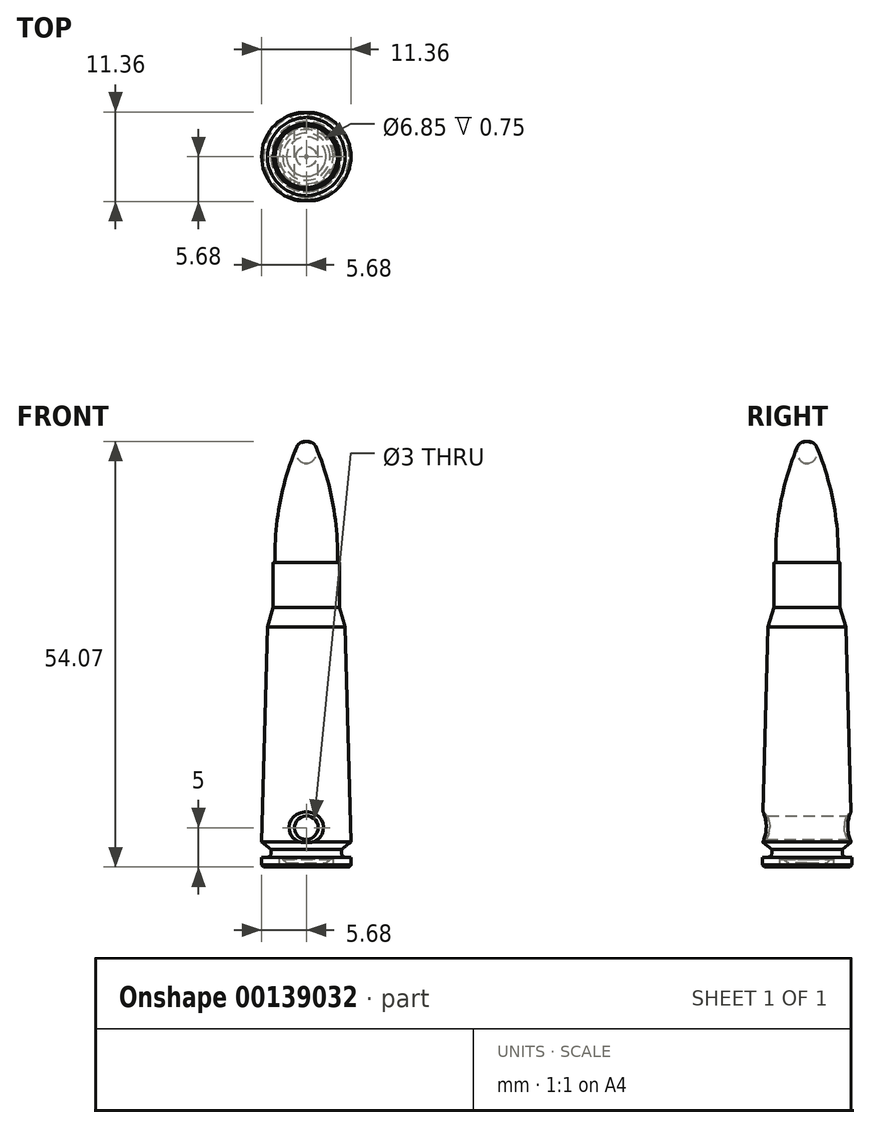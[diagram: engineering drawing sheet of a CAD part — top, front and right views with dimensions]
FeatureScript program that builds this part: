
annotation { "Feature Type Name" : "Feature", "Feature Type Description" : "" }
export const myFeature = defineFeature(function(context is Context, id is Id, definition is map)
    precondition{}
    {
        {
            var Q0;
            Q0=qCreatedBy(makeId("Front.planeOp"),FACE);
            var sketch = newSketch(context, id + "F0", { "sketchPlane" : qUnion([Q0])});
            skLineSegment(sketch, "E0", {"start": v(-11.63, 0) * mm, "end": v(20.36, 0) * mm, "construction": true});
            skLineSegment(sketch, "E1", {"start": v(0, -4.88) * mm, "end": v(0, 19.51) * mm, "construction": true});
            skLineSegment(sketch, "E2", {"start": v(0, 0) * mm, "end": v(-5.42, 0) * mm});
            skLineSegment(sketch, "E3", {"start": v(-5.42, 0) * mm, "end": v(-5.68, 0.25) * mm});
            skLineSegment(sketch, "E4", {"start": v(-5.68, 0.25) * mm, "end": v(-5.68, 1.25) * mm});
            skLineSegment(sketch, "E5", {"start": v(-5.68, 1.25) * mm, "end": v(-4.48, 1.25) * mm});
            skLineSegment(sketch, "E6", {"start": v(-4.48, 1.25) * mm, "end": v(-4.48, 2.25) * mm});
            skLineSegment(sketch, "E7", {"start": v(-4.48, 2.25) * mm, "end": v(-5.68, 3.2) * mm});
            skLineSegment(sketch, "E8", {"start": v(-5.68, 3.2) * mm, "end": v(-4.94, 30.5) * mm});
            skLineSegment(sketch, "E9", {"start": v(-4.94, 30.5) * mm, "end": v(-4.2, 33) * mm});
            skLineSegment(sketch, "E10", {"start": v(-4.2, 33) * mm, "end": v(-4.2, 38.7) * mm});
            skLineSegment(sketch, "E11", {"start": v(-4.2, 38.7) * mm, "end": v(0, 38.7) * mm});
            skLineSegment(sketch, "E12", {"start": v(0, 19.51) * mm, "end": v(0, 41.42) * mm, "construction": true});
            skLineSegment(sketch, "E13", {"start": v(0, 38.7) * mm, "end": v(0, 0) * mm});
            skPoint(sketch, "E14", {"position": v(0, 47.28) * mm});
            skLineSegment(sketch, "E15", {"start": v(0, 47.28) * mm, "end": v(-8.27, 19.19) * mm, "construction": true});
            skArc(sketch, "E16", {"start": v(-1.09, 53.7) * mm, "mid": v(-3.34, 46.35) * mm, "end": v(-3.96, 38.7) * mm});
            skLineSegment(sketch, "E17", {"start": v(0, 38.7) * mm, "end": v(0, 56) * mm});
            skLineSegment(sketch, "E18", {"start": v(-3.42, 0) * mm, "end": v(-3.42, 1) * mm});
            skLineSegment(sketch, "E19", {"start": v(-3.42, 1) * mm, "end": v(-2.5, 1) * mm});
            skLineSegment(sketch, "E20", {"start": v(-2.5, 1) * mm, "end": v(-2.5, 0) * mm});
            skPoint(sketch, "E21", {"position": v(0, 5) * mm});
            skCircle(sketch, "E22", {"center": v(0, 5) * mm, "radius": 1.5 * mm});
            skArc(sketch, "E23", {"start": v(-1.09, 53.7) * mm, "mid": v(-1.1, 53.68) * mm, "end": v(-1.1, 53.66) * mm});
            skArc(sketch, "E24", {"start": v(0, 54.07) * mm, "mid": v(-0.6, 53.98) * mm, "end": v(-1.1, 53.66) * mm});
            skSolve(sketch);
        }
        {
            var Q0;
            Q0=makeQuery(id+"F0.imprint","IMPRINT",FACE,{"disambiguationData":[TD([[makeQuery(id+"F0.imprint","IMPRINT",EDGE,{"derivedFrom":sQuery(id+"F0.wireOp",EDGE,"E2")}),-1.0]])]});
            var Q1;
            {var subQ2=sQuery(id+"F0.wireOp",EDGE,"E16");Q1=makeQuery(id+"F0.imprint","IMPRINT",FACE,{"disambiguationData":[TD([[makeQuery(id+"F0.imprint","IMPRINT",EDGE,{"derivedFrom":subQ2}),1.0]])]});}
            var Q2;
            Q2=sQuery(id+"F0.wireOp",EDGE,"E13");
            revolve(context, id + "F1", {"entities" : qUnion([Q0, Q1]), "axis" : qUnion([Q2]), "revolveType" : RevolveType.FULL});
        }
        {
            var Q0;
            Q0=makeQuery(id+"F1.opRevolve","SWEPT_EDGE",EDGE,{"disambiguationData":[OSD([sQuery(id+"F0.wireOp",EDGE,"E2"),sQuery(id+"F0.wireOp",EDGE,"E18")])]});
            chamfer(context, id + "F2", {"entities" : qUnion([Q0]), "width" : .25 * mm, "tangentPropagation" : true});
        }
        {
            var Q0;
            Q0=makeQuery(id+"F1.opRevolve","SWEPT_EDGE",EDGE,{"disambiguationData":[OSD([sQuery(id+"F0.wireOp",EDGE,"E19"),sQuery(id+"F0.wireOp",EDGE,"E20")])]});
            chamfer(context, id + "F3", {"entities" : qUnion([Q0]), "width" : .5 * mm, "tangentPropagation" : true});
        }
        {
            var Q0;
            {var subQ0=sQuery(id+"F0.wireOp",EDGE,"E22");var subQ1=sQuery(id+"F0.wireOp",EDGE,"E13");var subQ2=makeQuery(id+"F0.imprint","INTERSECT",VERTEX,{"disambiguationData":[OD(0.0)],"derivedFrom":[subQ1,subQ0]});Q0=makeQuery(id+"F0.imprint","IMPRINT",FACE,{"disambiguationData":[TD([[makeQuery(id+"F0.imprint","IMPRINT",EDGE,{"disambiguationData":[TD([[subQ2,-1.0]])],"derivedFrom":subQ1}),1.0]])]});}
            var Q1;
            {var subQ0=sQuery(id+"F0.wireOp",EDGE,"E22");var subQ1=sQuery(id+"F0.wireOp",EDGE,"E13");var subQ2=makeQuery(id+"F0.imprint","INTERSECT",VERTEX,{"disambiguationData":[OD(0.0)],"derivedFrom":[subQ1,subQ0]});Q1=makeQuery(id+"F0.imprint","IMPRINT",FACE,{"disambiguationData":[TD([[makeQuery(id+"F0.imprint","IMPRINT",EDGE,{"disambiguationData":[TD([[subQ2,-1.0]])],"derivedFrom":subQ1}),-1.0]])]});}
            var Q2;
            Q2=sQuery(id+"F0.wireOp",EDGE,"E22");
            extrude(context, id + "F4", {"entities" : qUnion([Q0, Q1]), "operationType" : NewBodyOperationType.REMOVE, "surfaceEntities" : qUnion([Q2]), "endBound" : BoundingType.SYMMETRIC, "depth" : 25 * mm});
        }
        {
            var Q0;
            Q0=makeQuery(id+"F4.boolean.opBoolean","INTERSECT",EDGE,{"disambiguationData":[OD(1.0)],"derivedFrom":[makeQuery(id+"F1.opRevolve","SWEPT_FACE",FACE,{"disambiguationData":[OSD([sQuery(id+"F0.wireOp",EDGE,"E8")])]}),makeQuery(id+"F4.opExtrude","SWEPT_FACE",FACE,{"disambiguationData":[OSD([sQuery(id+"F0.wireOp",EDGE,"E22")])]})]});
            var Q1;
            Q1=makeQuery(id+"F4.boolean.opBoolean","INTERSECT",EDGE,{"disambiguationData":[OD(0.0)],"derivedFrom":[makeQuery(id+"F1.opRevolve","SWEPT_FACE",FACE,{"disambiguationData":[OSD([sQuery(id+"F0.wireOp",EDGE,"E8")])]}),makeQuery(id+"F4.opExtrude","SWEPT_FACE",FACE,{"disambiguationData":[OSD([sQuery(id+"F0.wireOp",EDGE,"E22")])]})]});
            chamfer(context, id + "F5", {"entities" : qUnion([Q0, Q1]), "width" : .5 * mm, "tangentPropagation" : true});
        }
        {
            var Q0;
            Q0=makeQuery(id+"F1.opRevolve","SWEPT_EDGE",EDGE,{"disambiguationData":[OSD([sQuery(id+"F0.wireOp",EDGE,"E5"),sQuery(id+"F0.wireOp",EDGE,"E6")])]});
            fillet(context, id + "F6", {"entities" : qUnion([Q0]), "radius" : .5 * mm, "tangentPropagation" : true, "allowEdgeOverflow" : false});
        }
        {
            var Q0;
            Q0=makeQuery(id+"F1.opRevolve","SWEPT_EDGE",EDGE,{"disambiguationData":[OSD([sQuery(id+"F0.wireOp",EDGE,"E11"),sQuery(id+"F0.wireOp",EDGE,"E16")])]});
            fillet(context, id + "F7", {"entities" : qUnion([Q0]), "radius" : .25 * mm, "tangentPropagation" : true, "allowEdgeOverflow" : false});
        }
        {
            var Q0;
            Q0=makeQuery(id+"F1.opRevolve","SWEPT_EDGE",EDGE,{"disambiguationData":[OSD([sQuery(id+"F0.wireOp",EDGE,"E16"),sQuery(id+"F0.wireOp",EDGE,"E23"),sQuery(id+"F0.wireOp",EDGE,"E24")])]});
            fillet(context, id + "F8", {"entities" : qUnion([Q0]), "radius" : 1 * mm, "tangentPropagation" : true, "allowEdgeOverflow" : false});
        }
    });
